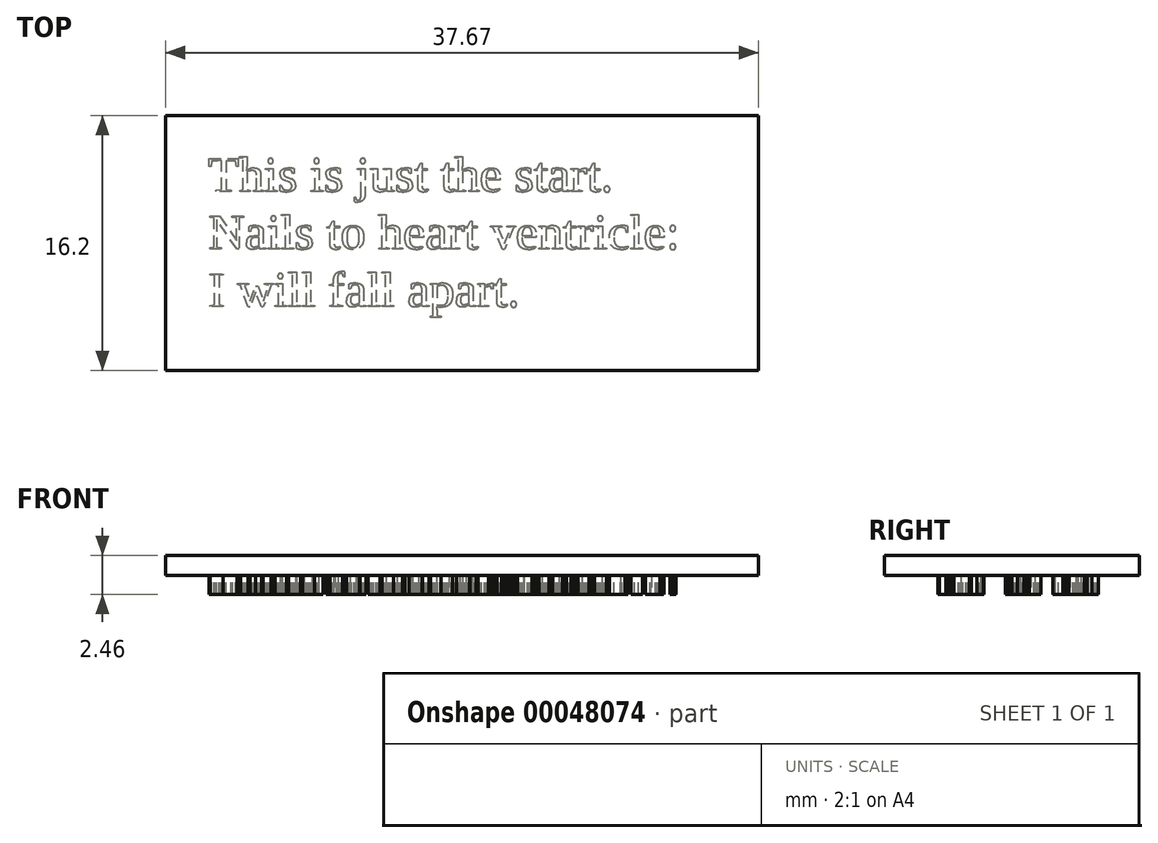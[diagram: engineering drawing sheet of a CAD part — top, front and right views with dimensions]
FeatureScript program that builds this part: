
annotation { "Feature Type Name" : "Feature", "Feature Type Description" : "" }
export const myFeature = defineFeature(function(context is Context, id is Id, definition is map)
    precondition{}
    {
        {
            var Q0;
            Q0=qCreatedBy(makeId("Top.planeOp"),FACE);
            var sketch = newSketch(context, id + "F0", { "sketchPlane" : qUnion([Q0])});
            skText(sketch, "E0", { "text": "This is just the start.\nNails to heart ventricle:\nI will fall apart. ", "fontName": "Tinos-Regular.ttf"});
            const initialGuessF0  = {"E0": [0.00116, 0.01138, 1, 0, 0.00229]};
            skSetInitialGuess(sketch, initialGuessF0);
            skSolve(sketch);
        }
        {
            var Q0;
            Q0=qCreatedBy(makeId("Top.planeOp"),FACE);
            var sketch = newSketch(context, id + "F1", { "sketchPlane" : qUnion([Q0])});
            skLineSegment(sketch, "E1.bottom", {"start": v(0, 0) * mm, "end": v(36.1, 0) * mm});
            skLineSegment(sketch, "E1.top", {"start": v(-1.57, 16.2) * mm, "end": v(36.1, 16.2) * mm});
            skLineSegment(sketch, "E1.left", {"start": v(-1.57, 0) * mm, "end": v(-1.57, 16.2) * mm});
            skLineSegment(sketch, "E1.right", {"start": v(36.1, 0) * mm, "end": v(36.1, 16.2) * mm});
            skLineSegment(sketch, "E2", {"start": v(0, 0) * mm, "end": v(-1.57, 0) * mm});
            skSolve(sketch);
        }
        {
            var Q0;
            Q0 = qSketchRegion(id + "F1", true);
            extrude(context, id + "F2", {"entities" : qUnion([Q0]), "depth" : 1.27 * mm});
        }
        {
            var Q0;
            Q0 = qSketchRegion(id + "F0", true);
            extrude(context, id + "F3", {"entities" : qUnion([Q0]), "operationType" : NewBodyOperationType.ADD, "oppositeDirection" : true, "depth" : 1.2 * mm});
        }
    });
